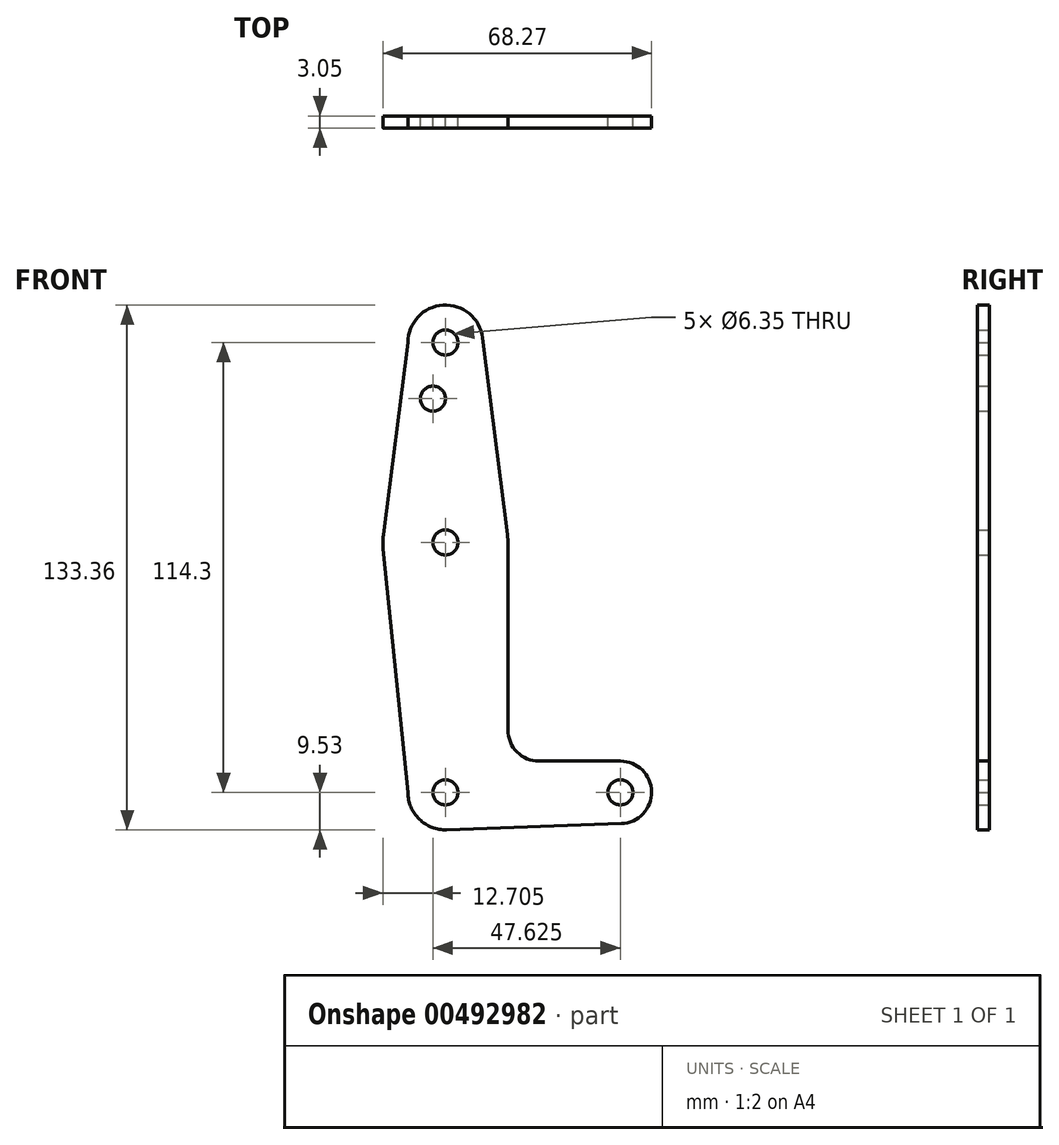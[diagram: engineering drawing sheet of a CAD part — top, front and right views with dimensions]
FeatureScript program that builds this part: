
annotation { "Feature Type Name" : "Feature", "Feature Type Description" : "" }
export const myFeature = defineFeature(function(context is Context, id is Id, definition is map)
    precondition{}
    {
        {
            var Q0;
            Q0=qCreatedBy(makeId("Front.planeOp"),FACE);
            var sketch = newSketch(context, id + "F0", { "sketchPlane" : qUnion([Q0])});
            skCircle(sketch, "E0", {"center": v(0, 114.3) * mm, "radius": 9.52 * mm});
            skLineSegment(sketch, "E1", {"start": v(0, 114.3) * mm, "end": v(0, 0) * mm, "construction": true});
            skCircle(sketch, "E2", {"center": v(0, 63.5) * mm, "radius": 15.88 * mm});
            skCircle(sketch, "E3", {"center": v(0, 0) * mm, "radius": 9.52 * mm});
            skLineSegment(sketch, "E4", {"start": v(0, 0) * mm, "end": v(44.45, 0) * mm});
            skCircle(sketch, "E5", {"center": v(44.45, 0) * mm, "radius": 7.94 * mm});
            skLineSegment(sketch, "E6", {"start": v(-9.52, 114.3) * mm, "end": v(-16, 63.5) * mm});
            skLineSegment(sketch, "E7", {"start": v(9.45, 115.5) * mm, "end": v(15.75, 65.48) * mm});
            skLineSegment(sketch, "E8", {"start": v(23.83, 7.94) * mm, "end": v(44.45, 7.94) * mm});
            skLineSegment(sketch, "E9", {"start": v(0.34, -9.52) * mm, "end": v(44.73, -7.93) * mm});
            skCircle(sketch, "E10", {"center": v(0, 114.3) * mm, "radius": 3.18 * mm});
            skCircle(sketch, "E11", {"center": v(-3.17, 100.03) * mm, "radius": 3.18 * mm});
            skCircle(sketch, "E12", {"center": v(0, 63.5) * mm, "radius": 3.18 * mm});
            skLineSegment(sketch, "E13", {"start": v(15.88, 63.5) * mm, "end": v(15.88, 15.89) * mm});
            skLineSegment(sketch, "E14", {"start": v(-15.8, 61.9) * mm, "end": v(-9.52, 0) * mm});
            skCircle(sketch, "E15", {"center": v(0, 0) * mm, "radius": 3.18 * mm});
            skCircle(sketch, "E16", {"center": v(44.45, 0) * mm, "radius": 3.18 * mm});
            skArc(sketch, "E17.filletArc", {"start": v(15.88, 15.89) * mm, "mid": v(18.2, 10.27) * mm, "end": v(23.83, 7.94) * mm});
            skSolve(sketch);
        }
        {
            var Q0;
            {var subQ0=sQuery(id+"F0.wireOp",EDGE,"E13");var subQ1=sQuery(id+"F0.wireOp",EDGE,"E2");var subQ2=makeQuery(id+"F0.imprint","INTERSECT",VERTEX,{"disambiguationData":[OD(0.0)],"derivedFrom":[subQ1,subQ0]});Q0=makeQuery(id+"F0.imprint","IMPRINT",FACE,{"disambiguationData":[TD([[makeQuery(id+"F0.imprint","IMPRINT",EDGE,{"disambiguationData":[TD([[subQ2,1.0]])],"derivedFrom":subQ1}),1.0]])]});}
            var Q1;
            Q1=makeQuery(id+"F0.imprint","IMPRINT",FACE,{"disambiguationData":[TD([[makeQuery(id+"F0.imprint","IMPRINT",EDGE,{"derivedFrom":sQuery(id+"F0.wireOp",EDGE,"E10")}),-1.0]])]});
            var Q2;
            {var subQ0=sQuery(id+"F0.wireOp",EDGE,"E7");Q2=makeQuery(id+"F0.imprint","IMPRINT",FACE,{"disambiguationData":[TD([[makeQuery(id+"F0.imprint","IMPRINT",EDGE,{"derivedFrom":subQ0}),-1.0]])]});}
            var Q3;
            Q3=makeQuery(id+"F0.imprint","IMPRINT",FACE,{"disambiguationData":[TD([[makeQuery(id+"F0.imprint","IMPRINT",EDGE,{"derivedFrom":sQuery(id+"F0.wireOp",EDGE,"E15")}),-1.0]])]});
            var Q4;
            {var subQ0=sQuery(id+"F0.wireOp",EDGE,"E9");Q4=makeQuery(id+"F0.imprint","IMPRINT",FACE,{"disambiguationData":[TD([[makeQuery(id+"F0.imprint","IMPRINT",EDGE,{"derivedFrom":subQ0}),1.0]])]});}
            var Q5;
            Q5=makeQuery(id+"F0.imprint","IMPRINT",FACE,{"disambiguationData":[TD([[makeQuery(id+"F0.imprint","IMPRINT",EDGE,{"derivedFrom":sQuery(id+"F0.wireOp",EDGE,"E12")}),-1.0]])]});
            var Q6;
            {var subQ0=sQuery(id+"F0.wireOp",EDGE,"E8");Q6=makeQuery(id+"F0.imprint","IMPRINT",FACE,{"disambiguationData":[TD([[makeQuery(id+"F0.imprint","IMPRINT",EDGE,{"derivedFrom":subQ0}),-1.0]])]});}
            var Q7;
            Q7=makeQuery(id+"F0.imprint","IMPRINT",FACE,{"disambiguationData":[TD([[makeQuery(id+"F0.imprint","IMPRINT",EDGE,{"derivedFrom":sQuery(id+"F0.wireOp",EDGE,"E16")}),-1.0]])]});
            extrude(context, id + "F1", {"entities" : qUnion([Q0, Q1, Q2, Q3, Q4, Q5, Q6, Q7]), "depth" : 3.05 * mm});
        }
    });
